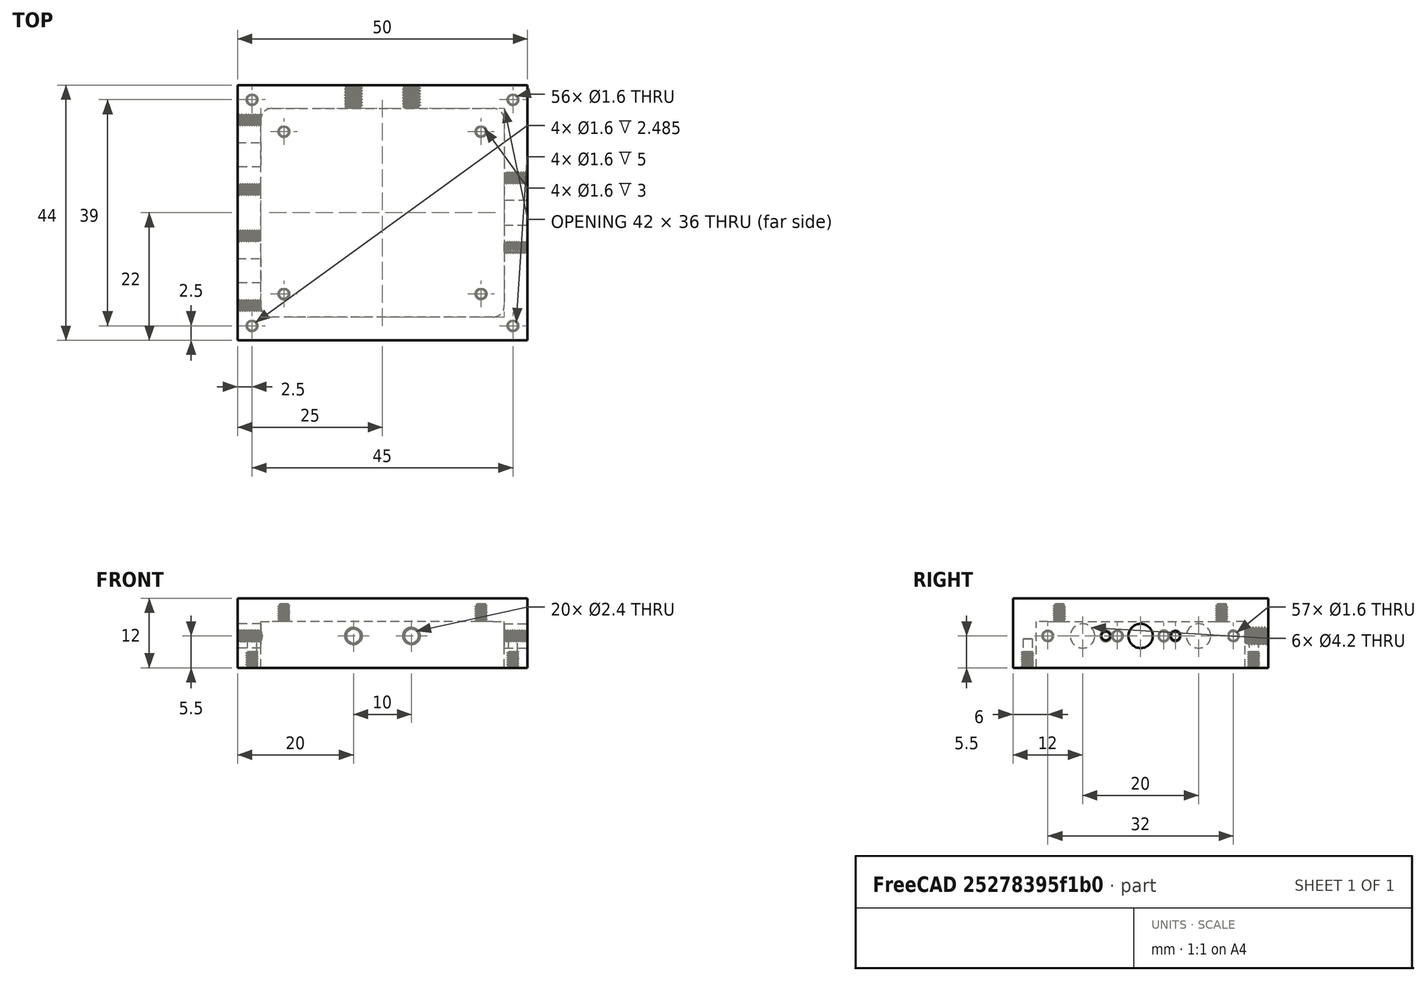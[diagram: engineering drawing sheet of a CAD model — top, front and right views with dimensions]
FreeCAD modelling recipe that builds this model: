
FCSTD DOCUMENT  (FreeCAD 0.19R24291 (Git))
Label: shell
License: All rights reserved
LicenseURL: http://en.wikipedia.org/wiki/All_rights_reserved
objects: TechDraw::DrawViewDimension×31, Part::FeaturePython×16, Sketcher::SketchObject×8, PartDesign::Pocket×7, TechDraw::DrawProjGroupItem×4, Part::MultiFuse×3, PartDesign::Pad×1, PartDesign::Body×1, TechDraw::DrawSVGTemplate×1, TechDraw::DrawProjGroup×1, TechDraw::DrawViewSection×1, TechDraw::DrawPage×1, Part::Cut×1
note: 45 computed .brp shape members not serialized (recipe doc carries the construction recipe); baked Part::Feature solids carry a one-line shape summary decoded from their .brp

FEATURE [Sketcher::SketchObject] Sketch
  FullyConstrained = true
  MapMode = 5
  Support = -> [XY_Plane]
  sketch-geometry (4):
    g0: LineSegment StartX=0 StartY=0 StartZ=0 EndX=50 EndY=0 EndZ=0
    g1: LineSegment StartX=50 StartY=0 StartZ=0 EndX=50 EndY=-44 EndZ=0
    g2: LineSegment StartX=50 StartY=-44 StartZ=0 EndX=0 EndY=-44 EndZ=0
    g3: LineSegment StartX=0 StartY=-44 StartZ=0 EndX=0 EndY=0 EndZ=0
  constraints (11):
    c: Coincident(g0,g1)
    c: Coincident(g1,g2)
    c: Coincident(g2,g3)
    c: Coincident(g3,g0)
    c: Horizontal(g0)
    c: Horizontal(g2)
    c: Vertical(g1)
    c: Vertical(g3)
    c: Coincident(g0,g-1)
    c: DistanceX(g2,g2) = 50
    c: DistanceY(g1,g1) = 44
FEATURE [PartDesign::Pad] Pad
  Direction = (1,1,1)
  Length = 12
  Length2 = 100
  Profile = -> Sketch
  Type = 0
FEATURE [Sketcher::SketchObject] Sketch001
  FullyConstrained = true
  MapMode = 5
  Support = -> [XY_Plane]
  sketch-geometry (8):
    g0: LineSegment StartX=6 StartY=-4 StartZ=0 EndX=44 EndY=-4 EndZ=0
    g1: LineSegment StartX=46 StartY=-6 StartZ=0 EndX=46 EndY=-38 EndZ=0
    g2: LineSegment StartX=44 StartY=-40 StartZ=0 EndX=6 EndY=-40 EndZ=0
    g3: LineSegment StartX=4 StartY=-38 StartZ=0 EndX=4 EndY=-6 EndZ=0
    g4: ArcOfCircle CenterX=6 CenterY=-6 CenterZ=0 NormalX=0 NormalY=0 NormalZ=1 AngleXU=0 Radius=2 StartAngle=1.5708 EndAngle=3.14159
    g5: ArcOfCircle CenterX=44 CenterY=-6 CenterZ=0 NormalX=0 NormalY=0 NormalZ=1 AngleXU=0 Radius=2 StartAngle=0 EndAngle=1.5708
    g6: ArcOfCircle CenterX=44 CenterY=-38 CenterZ=0 NormalX=0 NormalY=0 NormalZ=1 AngleXU=0 Radius=2 StartAngle=4.71239 EndAngle=6.28319
    g7: ArcOfCircle CenterX=6 CenterY=-38 CenterZ=0 NormalX=0 NormalY=0 NormalZ=1 AngleXU=0 Radius=2 StartAngle=3.14159 EndAngle=4.71239
  constraints (20):
    c: Horizontal(g0)
    c: Horizontal(g2)
    c: Vertical(g1)
    c: Vertical(g3)
    c: Tangent(g0,g4) = 1.5708
    c: Tangent(g3,g4) = 1.5708
    c: Tangent(g0,g5) = 1.5708
    c: Tangent(g1,g5) = 1.5708
    c: Tangent(g1,g6) = 1.5708
    c: Tangent(g2,g6) = 1.5708
    c: Tangent(g2,g7) = 1.5708
    c: Tangent(g3,g7) = 1.5708
    c: Radius(g5) = 2
    c: Radius(g6) = 2
    c: Radius(g4) = 2
    c: Radius(g7) = 2
    c: DistanceX(g3) = 4
    c: DistanceY(g0) = -4
    c: DistanceX(g1) = 46
    c: DistanceY(g2) = -40
FEATURE [PartDesign::Pocket] Pocket
  BaseFeature = -> Pad
  Length = 8
  Length2 = 100
  Profile = -> Sketch001
  Reversed = true
  Type = 0
FEATURE [Sketcher::SketchObject] Sketch011
  FullyConstrained = true
  MapMode = 5
  Placement = pos=(0,0,0) rot=(0.57735,0.57735,0.57735;2.0944rad)
  Support = -> [YZ_Plane]
  sketch-geometry (2):
    g0: Circle CenterX=-32 CenterY=5.5 CenterZ=0 NormalX=0 NormalY=0 NormalZ=1 AngleXU=0 Radius=2.1
    g1: Circle CenterX=-12 CenterY=5.5 CenterZ=0 NormalX=0 NormalY=0 NormalZ=1 AngleXU=0 Radius=2.1
  constraints (6):
    c: Diameter(g0) = 4.2
    c: DistanceY(g0) = 5.5
    c: DistanceY(g1) = 5.5
    c: DistanceX(g1) = -12
    c: DistanceX(g0) = -32
    c: Diameter(g1) = 4.2
FEATURE [PartDesign::Pocket] Pocket001
  BaseFeature = -> Pocket
  Length = 0
  Length2 = 100
  Profile = -> Sketch011
  Reversed = true
  Type = 3
  UpToFace = -> Pocket [Face7]
FEATURE [Sketcher::SketchObject] Sketch012
  FullyConstrained = true
  MapMode = 5
  Placement = pos=(0,0,0) rot=(0.57735,-0.57735,-0.57735;2.0944rad)
  Support = -> [Pocket001]
  sketch-geometry (4):
    g0: Circle CenterX=6 CenterY=5.5 CenterZ=0 NormalX=0 NormalY=0 NormalZ=1 AngleXU=0 Radius=0.8
    g1: Circle CenterX=18 CenterY=5.5 CenterZ=0 NormalX=0 NormalY=0 NormalZ=1 AngleXU=0 Radius=0.8
    g2: Circle CenterX=26 CenterY=5.5 CenterZ=0 NormalX=0 NormalY=0 NormalZ=1 AngleXU=0 Radius=0.8
    g3: Circle CenterX=38 CenterY=5.5 CenterZ=0 NormalX=0 NormalY=0 NormalZ=1 AngleXU=0 Radius=0.8
  constraints (12):
    c: Diameter(g0) = 1.6
    c: Diameter(g1) = 1.6
    c: Diameter(g2) = 1.6
    c: Diameter(g3) = 1.6
    c: DistanceY(g0) = 5.5
    c: DistanceY(g1) = 5.5
    c: DistanceY(g2) = 5.5
    c: DistanceY(g3) = 5.5
    c: DistanceX(g0,g1) = 12
    c: DistanceX(g2,g3) = 12
    c: DistanceX(g1,g2) = 8
    c: DistanceX(g0) = 6
FEATURE [PartDesign::Pocket] Pocket002
  BaseFeature = -> Pocket001
  Length = 5
  Length2 = 100
  Profile = -> Sketch012
  Type = 0
FEATURE [Sketcher::SketchObject] Sketch013
  FullyConstrained = true
  MapMode = 5
  Placement = pos=(50,0,0) rot=(0.57735,0.57735,0.57735;2.0944rad)
  Support = -> [Pocket002]
  sketch-geometry (3):
    g0: Circle CenterX=-22 CenterY=5.5 CenterZ=0 NormalX=0 NormalY=0 NormalZ=1 AngleXU=0 Radius=2.1
    g1: Circle CenterX=-28 CenterY=5.5 CenterZ=0 NormalX=0 NormalY=0 NormalZ=1 AngleXU=0 Radius=0.75
    g2: Circle CenterX=-16 CenterY=5.5 CenterZ=0 NormalX=0 NormalY=0 NormalZ=1 AngleXU=0 Radius=0.8
  constraints (9):
    c: Diameter(g0) = 4.2
    c: Diameter(g2) = 1.6
    c: Diameter(g1) = 1.5
    c: DistanceY(g1) = 5.5
    c: DistanceY(g0) = 5.5
    c: DistanceY(g2) = 5.5
    c: DistanceX(g1,g2) = 12
    c: DistanceX(g0,g2) = 6
    c: DistanceX(g0) = -22
FEATURE [PartDesign::Pocket] Pocket003
  BaseFeature = -> Pocket002
  Length = 4
  Length2 = 100
  Profile = -> Sketch013
  Type = 0
FEATURE [Sketcher::SketchObject] Sketch015
  FullyConstrained = true
  MapMode = 5
  Support = -> [XY_Plane]
  sketch-geometry (4):
    g0: Circle CenterX=2.5 CenterY=-2.5 CenterZ=0 NormalX=0 NormalY=0 NormalZ=1 AngleXU=0 Radius=0.8
    g1: Circle CenterX=2.5 CenterY=-41.5 CenterZ=0 NormalX=0 NormalY=0 NormalZ=1 AngleXU=0 Radius=0.8
    g2: Circle CenterX=47.5 CenterY=-41.5 CenterZ=0 NormalX=0 NormalY=0 NormalZ=1 AngleXU=0 Radius=0.8
    g3: Circle CenterX=47.5 CenterY=-2.5 CenterZ=0 NormalX=0 NormalY=0 NormalZ=1 AngleXU=0 Radius=0.8
  constraints (12):
    c: Diameter(g0) = 1.6
    c: Diameter(g1) = 1.6
    c: Diameter(g2) = 1.6
    c: Diameter(g3) = 1.6
    c: DistanceX(g0) = 2.5
    c: DistanceY(g0) = -2.5
    c: DistanceY(g3) = -2.5
    c: DistanceX(g3) = 47.5
    c: DistanceY(g1) = -41.5
    c: DistanceX(g1) = 2.5
    c: DistanceX(g2) = 47.5
    c: DistanceY(g2) = -41.5
FEATURE [PartDesign::Pocket] Pocket005
  BaseFeature = -> Pocket003
  Length = 5
  Length2 = 100
  Profile = -> Sketch015
  Reversed = true
  Type = 0
FEATURE [Sketcher::SketchObject] Sketch017
  FullyConstrained = true
  MapMode = 5
  Placement = pos=(0,0,0) rot=(1,0,0;1.5708rad)
  Support = -> [XZ_Plane]
  sketch-geometry (2):
    g0: Circle CenterX=20 CenterY=5.5 CenterZ=0 NormalX=0 NormalY=0 NormalZ=1 AngleXU=0 Radius=1.2
    g1: Circle CenterX=30 CenterY=5.5 CenterZ=0 NormalX=0 NormalY=0 NormalZ=1 AngleXU=0 Radius=1.2
  constraints (6):
    c: Diameter(g0) = 2.4
    c: Diameter(g1) = 2.4
    c: DistanceY(g0) = 5.5
    c: DistanceY(g1) = 5.5
    c: DistanceX(g0,g1) = 10
    c: DistanceX(g0) = 20
FEATURE [PartDesign::Pocket] Pocket007
  BaseFeature = -> Pocket005
  Length = 4
  Length2 = 100
  Profile = -> Sketch017
  Reversed = true
  Type = 0
FEATURE [Sketcher::SketchObject] Sketch018
  FullyConstrained = true
  MapMode = 5
  Support = -> [XY_Plane]
  sketch-geometry (4):
    g0: Circle CenterX=8 CenterY=-36 CenterZ=0 NormalX=0 NormalY=0 NormalZ=1 AngleXU=0 Radius=0.8
    g1: Circle CenterX=42 CenterY=-36 CenterZ=0 NormalX=0 NormalY=0 NormalZ=1 AngleXU=0 Radius=0.8
    g2: Circle CenterX=8 CenterY=-8 CenterZ=0 NormalX=0 NormalY=0 NormalZ=1 AngleXU=0 Radius=0.8
    g3: Circle CenterX=42 CenterY=-8 CenterZ=0 NormalX=0 NormalY=0 NormalZ=1 AngleXU=0 Radius=0.8
  constraints (12):
    c: Diameter(g2) = 1.6
    c: Diameter(g3) = 1.6
    c: Diameter(g1) = 1.6
    c: Diameter(g0) = 1.6
    c: DistanceX(g0) = 8
    c: DistanceY(g0) = -36
    c: DistanceX(g1) = 42
    c: DistanceY(g1) = -36
    c: DistanceY(g2) = -8
    c: DistanceX(g2) = 8
    c: DistanceX(g3) = 42
    c: DistanceY(g3) = -8
FEATURE [PartDesign::Pocket] Pocket008
  BaseFeature = -> Pocket007
  Length = 11
  Length2 = 100
  Profile = -> Sketch018
  Reversed = true
  Type = 0
FEATURE [PartDesign::Body] Body
  Group = -> [Sketch,Pad,Sketch001,Pocket,Sketch011,Pocket001,Sketch012,Pocket002,Sketch013,Pocket003,Sketch015,Pocket005,Sketch017,Pocket007,Sketch018,Pocket008]
  Origin = -> Origin
  Tip = -> Pocket008
FEATURE [TechDraw::DrawSVGTemplate] Template
  EditableTexts = Designed_by_Name=YXK; FC-Date=2021/9/6; FC-Title=Title; Subtitle=DiffAD620_shell
  Height = 210
  Orientation = 1
  Width = 297
FEATURE [TechDraw::DrawProjGroupItem] ProjItem  label="Front"
  CoarseView = false
  Direction = (0,0,-1)
  Focus = 100
  HardHidden = false
  IsoCount = 0
  IsoHidden = false
  IsoVisible = false
  LockPosition = true
  Perspective = false
  Rotation = 0
  RotationVector = (1,0,0)
  Scale = 1.5
  ScaleType = 2
  SeamHidden = false
  SeamVisible = true
  SmoothHidden = false
  SmoothVisible = true
  Source = -> [Pocket008]
  Type = 0
  X = 0
  XDirection = (1,0,0)
  Y = 0
FEATURE [TechDraw::DrawProjGroupItem] ProjItem001  label="Left"
  CoarseView = false
  Direction = (-1,0,-1e-16)
  Focus = 100
  HardHidden = false
  IsoCount = 0
  IsoHidden = false
  IsoVisible = false
  LockPosition = false
  Perspective = false
  Rotation = 0
  RotationVector = (1,0,0)
  Scale = 1.5
  ScaleType = 2
  SeamHidden = false
  SeamVisible = true
  SmoothHidden = false
  SmoothVisible = true
  Source = -> [Pocket008]
  Type = 1
  X = 88.5544
  XDirection = (1e-16,0,-1)
  Y = 0
FEATURE [TechDraw::DrawProjGroupItem] ProjItem002  label="Right"
  CoarseView = false
  Direction = (1,0,-1e-16)
  Focus = 100
  HardHidden = false
  IsoCount = 0
  IsoHidden = false
  IsoVisible = false
  LockPosition = false
  Perspective = false
  Rotation = 0
  RotationVector = (1,0,0)
  Scale = 1.5
  ScaleType = 2
  SeamHidden = false
  SeamVisible = true
  SmoothHidden = false
  SmoothVisible = true
  Source = -> [Pocket008]
  Type = 2
  X = -87.7386
  XDirection = (1e-16,0,1)
  Y = 0
FEATURE [TechDraw::DrawProjGroupItem] ProjItem003  label="FrontTopRight"
  CoarseView = false
  Direction = (0.57735,-0.57735,-0.57735)
  Focus = 100
  HardHidden = false
  IsoCount = 0
  IsoHidden = false
  IsoVisible = false
  LockPosition = false
  Perspective = false
  Rotation = 0
  RotationVector = (1,0,0)
  Scale = 1.5
  ScaleType = 2
  SeamHidden = false
  SeamVisible = true
  SmoothHidden = false
  SmoothVisible = true
  Source = -> [Pocket008]
  Type = 7
  X = -105.359
  XDirection = (0.707107,0,0.707107)
  Y = -87.1945
FEATURE [TechDraw::DrawProjGroup] ProjGroup
  Anchor = -> ProjItem
  AutoDistribute = false
  LockPosition = false
  ProjectionType = 0
  Rotation = 0
  Scale = 1.5
  ScaleType = 2
  Source = -> [Pocket008]
  Views = -> [ProjItem,ProjItem001,ProjItem002,ProjItem003]
  X = 158.446
  Y = 149.013
  spacingX = 15
  spacingY = 15
FEATURE [TechDraw::DrawViewDimension] Dimension
  Arbitrary = false
  ArbitraryTolerances = false
  EqualTolerance = true
  FormatSpec = %.0f
  FormatSpecOverTolerance = %+.2f
  FormatSpecUnderTolerance = %+.2f
  Inverted = false
  LockPosition = false
  MeasureType = 1
  OverTolerance = 0
  References2D = -> [ProjItem]
  Rotation = 0
  ScaleType = 0
  TheoreticalExact = false
  Type = 1
  UnderTolerance = 0
  X = -1.51058
  Y = -14.761
FEATURE [TechDraw::DrawViewDimension] Dimension001
  Arbitrary = false
  ArbitraryTolerances = false
  EqualTolerance = true
  FormatSpec = %.0f
  FormatSpecOverTolerance = %+.2f
  FormatSpecUnderTolerance = %+.2f
  Inverted = false
  LockPosition = false
  MeasureType = 1
  OverTolerance = 0
  References2D = -> [ProjItem]
  Rotation = 0
  ScaleType = 0
  TheoreticalExact = false
  Type = 2
  UnderTolerance = 0
  X = 22.5074
  Y = 3.51417
FEATURE [TechDraw::DrawViewDimension] Dimension002
  Arbitrary = false
  ArbitraryTolerances = false
  EqualTolerance = true
  FormatSpec = %.0f
  FormatSpecOverTolerance = %+.2f
  FormatSpecUnderTolerance = %+.2f
  Inverted = false
  LockPosition = false
  MeasureType = 1
  OverTolerance = 0
  References2D = -> [ProjItem]
  Rotation = 0
  ScaleType = 0
  TheoreticalExact = false
  Type = 1
  UnderTolerance = 0
  X = -1.46443
  Y = -41.4304
FEATURE [TechDraw::DrawViewDimension] Dimension003
  Arbitrary = false
  ArbitraryTolerances = false
  EqualTolerance = true
  FormatSpec = %.0f
  FormatSpecOverTolerance = %+.2f
  FormatSpecUnderTolerance = %+.2f
  Inverted = false
  LockPosition = false
  MeasureType = 1
  OverTolerance = 0
  References2D = -> [ProjItem]
  Rotation = 0
  ScaleType = 0
  TheoreticalExact = false
  Type = 2
  UnderTolerance = 0
  X = 51.9622
  Y = -1.04489
FEATURE [TechDraw::DrawViewDimension] Dimension004
  Arbitrary = false
  ArbitraryTolerances = false
  EqualTolerance = true
  FormatSpec = %.0f
  FormatSpecOverTolerance = %+.2f
  FormatSpecUnderTolerance = %+.2f
  Inverted = false
  LockPosition = false
  MeasureType = 1
  OverTolerance = 0
  References2D = -> [ProjItem]
  Rotation = 0
  ScaleType = 0
  TheoreticalExact = false
  Type = 1
  UnderTolerance = 0
  X = -43.6818
  Y = -32.9738
FEATURE [TechDraw::DrawViewDimension] Dimension005
  Arbitrary = false
  ArbitraryTolerances = false
  EqualTolerance = true
  FormatSpec = %.0f
  FormatSpecOverTolerance = %+.2f
  FormatSpecUnderTolerance = %+.2f
  Inverted = false
  LockPosition = false
  MeasureType = 1
  OverTolerance = 0
  References2D = -> [ProjItem]
  Rotation = 0
  ScaleType = 0
  TheoreticalExact = false
  Type = 2
  UnderTolerance = 0
  X = 41.6799
  Y = -20.2635
FEATURE [TechDraw::DrawViewDimension] Dimension006
  Arbitrary = false
  ArbitraryTolerances = false
  EqualTolerance = true
  FormatSpec = %.0f
  FormatSpecOverTolerance = %+.2f
  FormatSpecUnderTolerance = %+.2f
  Inverted = false
  LockPosition = false
  MeasureType = 1
  OverTolerance = 0
  References2D = -> [ProjItem001]
  Rotation = 0
  ScaleType = 0
  TheoreticalExact = false
  Type = 1
  UnderTolerance = 0
  X = -0.151106
  Y = -46.1582
FEATURE [TechDraw::DrawViewDimension] Dimension007
  Arbitrary = false
  ArbitraryTolerances = false
  EqualTolerance = true
  FormatSpec = %.1f
  FormatSpecOverTolerance = %+.2f
  FormatSpecUnderTolerance = %+.2f
  Inverted = false
  LockPosition = false
  MeasureType = 1
  OverTolerance = 0
  References2D = -> [ProjItem]
  Rotation = 0
  ScaleType = 0
  TheoreticalExact = false
  Type = 1
  UnderTolerance = 0
  X = 27.4267
  Y = 44.2346
FEATURE [TechDraw::DrawViewDimension] Dimension008
  Arbitrary = false
  ArbitraryTolerances = false
  EqualTolerance = true
  FormatSpec = %.1f
  FormatSpecOverTolerance = %+.2f
  FormatSpecUnderTolerance = %+.2f
  Inverted = false
  LockPosition = false
  MeasureType = 1
  OverTolerance = 0
  References2D = -> [ProjItem]
  Rotation = 0
  ScaleType = 0
  TheoreticalExact = false
  Type = 2
  UnderTolerance = 0
  X = 42.6656
  Y = 25.7621
FEATURE [TechDraw::DrawViewDimension] Dimension009
  Arbitrary = false
  ArbitraryTolerances = false
  EqualTolerance = true
  FormatSpec = %.0f
  FormatSpecOverTolerance = %+.2f
  FormatSpecUnderTolerance = %+.2f
  Inverted = false
  LockPosition = false
  MeasureType = 1
  OverTolerance = 0
  References2D = -> [ProjItem]
  Rotation = 0
  ScaleType = 0
  TheoreticalExact = false
  Type = 1
  UnderTolerance = 0
  X = -27.8145
  Y = 16.2307
FEATURE [TechDraw::DrawViewDimension] Dimension010
  Arbitrary = false
  ArbitraryTolerances = false
  EqualTolerance = true
  FormatSpec = %.0f
  FormatSpecOverTolerance = %+.2f
  FormatSpecUnderTolerance = %+.2f
  Inverted = false
  LockPosition = false
  MeasureType = 1
  OverTolerance = 0
  References2D = -> [ProjItem]
  Rotation = 0
  ScaleType = 0
  TheoreticalExact = false
  Type = 2
  UnderTolerance = 0
  X = -19.6538
  Y = 26.0273
FEATURE [TechDraw::DrawViewDimension] Dimension011
  Arbitrary = false
  ArbitraryTolerances = false
  EqualTolerance = true
  FormatSpec = R%.0f
  FormatSpecOverTolerance = %+.2f
  FormatSpecUnderTolerance = %+.2f
  Inverted = false
  LockPosition = false
  MeasureType = 1
  OverTolerance = 0
  References2D = -> [ProjItem]
  Rotation = 0
  ScaleType = 0
  TheoreticalExact = false
  Type = 4
  UnderTolerance = 0
  X = -33.2413
  Y = 46.5037
FEATURE [TechDraw::DrawViewDimension] Dimension012
  Arbitrary = true
  ArbitraryTolerances = false
  EqualTolerance = true
  FormatSpec = 4xM2深3
  FormatSpecOverTolerance = %+.2f
  FormatSpecUnderTolerance = %+.2f
  Inverted = false
  LockPosition = false
  MeasureType = 1
  OverTolerance = 0
  References2D = -> [ProjItem]
  Rotation = 0
  ScaleType = 0
  TheoreticalExact = false
  Type = 5
  UnderTolerance = 0
  X = -57.0458
  Y = -14.32
FEATURE [TechDraw::DrawViewDimension] Dimension013
  Arbitrary = true
  ArbitraryTolerances = false
  EqualTolerance = true
  FormatSpec = 4xM2深3
  FormatSpecOverTolerance = %+.2f
  FormatSpecUnderTolerance = %+.2f
  Inverted = false
  LockPosition = false
  MeasureType = 1
  OverTolerance = 0
  References2D = -> [ProjItem]
  Rotation = 0
  ScaleType = 0
  TheoreticalExact = false
  Type = 5
  UnderTolerance = 0
  X = -58.3902
  Y = -2.55251
FEATURE [TechDraw::DrawViewDimension] Dimension014
  Arbitrary = false
  ArbitraryTolerances = false
  EqualTolerance = true
  FormatSpec = %.0f
  FormatSpecOverTolerance = %+.2f
  FormatSpecUnderTolerance = %+.2f
  Inverted = false
  LockPosition = false
  MeasureType = 1
  OverTolerance = 0
  References2D = -> [ProjItem002]
  Rotation = 0
  ScaleType = 0
  TheoreticalExact = false
  Type = 2
  UnderTolerance = 0
  X = -26.1138
  Y = -2.16784
FEATURE [TechDraw::DrawViewDimension] Dimension015
  Arbitrary = false
  ArbitraryTolerances = false
  EqualTolerance = true
  FormatSpec = %.0f
  FormatSpecOverTolerance = %+.2f
  FormatSpecUnderTolerance = %+.2f
  Inverted = false
  LockPosition = false
  MeasureType = 1
  OverTolerance = 0
  References2D = -> [ProjItem002]
  Rotation = 0
  ScaleType = 0
  TheoreticalExact = false
  Type = 2
  UnderTolerance = 0
  X = -19.1767
  Y = -2.33216
FEATURE [TechDraw::DrawViewDimension] Dimension016
  Arbitrary = false
  ArbitraryTolerances = false
  EqualTolerance = true
  FormatSpec = ⌀%.1f
  FormatSpecOverTolerance = %+.2f
  FormatSpecUnderTolerance = %+.2f
  Inverted = false
  LockPosition = false
  MeasureType = 1
  OverTolerance = 0
  References2D = -> [ProjItem002]
  Rotation = 0
  ScaleType = 0
  TheoreticalExact = false
  Type = 5
  UnderTolerance = 0
  X = 19.2938
  Y = 22.3288
FEATURE [TechDraw::DrawViewDimension] Dimension017
  Arbitrary = true
  ArbitraryTolerances = false
  EqualTolerance = true
  FormatSpec = 2xM2
  FormatSpecOverTolerance = %+.2f
  FormatSpecUnderTolerance = %+.2f
  Inverted = false
  LockPosition = false
  MeasureType = 1
  OverTolerance = 0
  References2D = -> [ProjItem002]
  Rotation = 0
  ScaleType = 0
  TheoreticalExact = false
  Type = 5
  UnderTolerance = 0
  X = 27.3148
  Y = 13.6574
FEATURE [TechDraw::DrawViewDimension] Dimension018
  Arbitrary = false
  ArbitraryTolerances = false
  EqualTolerance = true
  FormatSpec = %.0f
  FormatSpecOverTolerance = %+.2f
  FormatSpecUnderTolerance = %+.2f
  Inverted = false
  LockPosition = false
  MeasureType = 1
  OverTolerance = 0
  References2D = -> [ProjItem001]
  Rotation = 0
  ScaleType = 0
  TheoreticalExact = false
  Type = 2
  UnderTolerance = 0
  X = 29.6044
  Y = 15
FEATURE [TechDraw::DrawViewDimension] Dimension019
  Arbitrary = false
  ArbitraryTolerances = false
  EqualTolerance = true
  FormatSpec = %.0f
  FormatSpecOverTolerance = %+.2f
  FormatSpecUnderTolerance = %+.2f
  Inverted = false
  LockPosition = false
  MeasureType = 1
  OverTolerance = 0
  References2D = -> [ProjItem001]
  Rotation = 0
  ScaleType = 0
  TheoreticalExact = false
  Type = 2
  UnderTolerance = 0
  X = 18.4673
  Y = 0.825165
FEATURE [TechDraw::DrawViewDimension] Dimension020
  Arbitrary = false
  ArbitraryTolerances = false
  EqualTolerance = true
  FormatSpec = %.0f
  FormatSpecOverTolerance = %+.2f
  FormatSpecUnderTolerance = %+.2f
  Inverted = false
  LockPosition = false
  MeasureType = 1
  OverTolerance = 0
  References2D = -> [ProjItem001]
  Rotation = 0
  ScaleType = 0
  TheoreticalExact = false
  Type = 2
  UnderTolerance = 0
  X = 29.9083
  Y = -15.8782
FEATURE [TechDraw::DrawViewDimension] Dimension021
  Arbitrary = false
  ArbitraryTolerances = false
  EqualTolerance = true
  FormatSpec = %.0f
  FormatSpecOverTolerance = %+.2f
  FormatSpecUnderTolerance = %+.2f
  Inverted = false
  LockPosition = false
  MeasureType = 1
  OverTolerance = 0
  References2D = -> [ProjItem001]
  Rotation = 0
  ScaleType = 0
  TheoreticalExact = false
  Type = 2
  UnderTolerance = 0
  X = 18.1756
  Y = 11.9189
FEATURE [TechDraw::DrawViewDimension] Dimension022
  Arbitrary = false
  ArbitraryTolerances = false
  EqualTolerance = true
  FormatSpec = %.0f
  FormatSpecOverTolerance = %+.2f
  FormatSpecUnderTolerance = %+.2f
  Inverted = false
  LockPosition = false
  MeasureType = 1
  OverTolerance = 0
  References2D = -> [ProjItem001]
  Rotation = 0
  ScaleType = 0
  TheoreticalExact = false
  Type = 2
  UnderTolerance = 0
  X = 18.3011
  Y = -8.20297
FEATURE [TechDraw::DrawViewDimension] Dimension023
  Arbitrary = true
  ArbitraryTolerances = false
  EqualTolerance = true
  FormatSpec = 4xM2
  FormatSpecOverTolerance = %+.2f
  FormatSpecUnderTolerance = %+.2f
  Inverted = false
  LockPosition = false
  MeasureType = 1
  OverTolerance = 0
  References2D = -> [ProjItem001]
  Rotation = 0
  ScaleType = 0
  TheoreticalExact = false
  Type = 5
  UnderTolerance = 0
  X = -22.3308
  Y = 36.758
FEATURE [TechDraw::DrawViewDimension] Dimension024
  Arbitrary = false
  ArbitraryTolerances = false
  EqualTolerance = true
  FormatSpec = ⌀%.1f
  FormatSpecOverTolerance = %+.2f
  FormatSpecUnderTolerance = %+.2f
  Inverted = false
  LockPosition = false
  MeasureType = 1
  OverTolerance = 0
  References2D = -> [ProjItem001]
  Rotation = 0
  ScaleType = 0
  TheoreticalExact = false
  Type = 5
  UnderTolerance = 0
  X = -22.4562
  Y = 20.6999
FEATURE [TechDraw::DrawViewSection] SectionView  label="Section  - "
  BaseView = -> ProjItem
  CoarseView = false
  CutSurfaceDisplay = 2
  Direction = (0,-1,0)
  FileGeomPattern = <path>
  FileHatchPattern = <path>
  Focus = 100
  FuseBeforeCut = false
  HardHidden = false
  HatchScale = 1
  IsoCount = 0
  IsoHidden = false
  IsoVisible = false
  LockPosition = false
  NameGeomPattern = Diamond
  Perspective = false
  Rotation = 0
  Scale = 1.5
  ScaleType = 0
  SeamHidden = false
  SeamVisible = true
  SectionDirection = 3
  SectionNormal = (0,-1,0)
  SectionOrigin = (25,-17,6)
  SmoothHidden = false
  SmoothVisible = true
  Source = -> [Pocket008]
  X = 158.197
  XDirection = (1,0,0)
  Y = 79.0756
FEATURE [TechDraw::DrawViewDimension] Dimension025
  Arbitrary = false
  ArbitraryTolerances = false
  EqualTolerance = true
  FormatSpec = %.0f
  FormatSpecOverTolerance = %+.2f
  FormatSpecUnderTolerance = %+.2f
  Inverted = false
  LockPosition = false
  MeasureType = 1
  OverTolerance = 0
  References2D = -> [SectionView]
  Rotation = 0
  ScaleType = 0
  TheoreticalExact = false
  Type = 2
  UnderTolerance = 0
  X = 43.1667
  Y = -1.20794
FEATURE [Part::FeaturePython] ThreadedRod  label="M2x3.0-ThreadedRod"  # Fasteners workbench fastener (typed FeaturePython)
  Placement = pos=(47.5,-41.5,0) rot=(-1,0,0;3.14159rad)
  baseObject = -> Body [Edge18]
  diameter = 2
  invert = true
  length = 3
  matchOuter = false
  offset = 0
  thread = true
FEATURE [Part::FeaturePython] ThreadedRod001  label="M2x3.0-ThreadedRod008"  # Fasteners workbench fastener (typed FeaturePython)
  Placement = pos=(47.5,-2.5,0) rot=(-1,0,0;3.14159rad)
  baseObject = -> Body [Edge28]
  diameter = 2
  invert = true
  length = 3
  matchOuter = false
  offset = 0
  thread = true
FEATURE [Part::FeaturePython] ThreadedRod002  label="M2x3.0-ThreadedRod009"  # Fasteners workbench fastener (typed FeaturePython)
  Placement = pos=(42,-8,8) rot=(-1,0,0;3.14159rad)
  baseObject = -> Body [Edge90]
  diameter = 2
  invert = false
  length = 3
  matchOuter = false
  offset = 0
  thread = true
FEATURE [Part::FeaturePython] ThreadedRod003  label="M2x3.0-ThreadedRod010"  # Fasteners workbench fastener (typed FeaturePython)
  Placement = pos=(42,-36,8) rot=(-1,0,0;3.14159rad)
  baseObject = -> Body [Edge88]
  diameter = 2
  invert = false
  length = 3
  matchOuter = false
  offset = 0
  thread = true
FEATURE [Part::FeaturePython] ThreadedRod004  label="M2x3.0-ThreadedRod011"  # Fasteners workbench fastener (typed FeaturePython)
  Placement = pos=(8,-36,8) rot=(-1,0,0;3.14159rad)
  baseObject = -> Body [Edge89]
  diameter = 2
  invert = false
  length = 3
  matchOuter = false
  offset = 0
  thread = true
FEATURE [Part::FeaturePython] ThreadedRod005  label="M2x3.0-ThreadedRod012"  # Fasteners workbench fastener (typed FeaturePython)
  Placement = pos=(8,-8,8) rot=(-1,0,0;3.14159rad)
  baseObject = -> Body [Edge91]
  diameter = 2
  invert = false
  length = 3
  matchOuter = false
  offset = 0
  thread = true
FEATURE [Part::FeaturePython] ThreadedRod006  label="M2x3.0-ThreadedRod013"  # Fasteners workbench fastener (typed FeaturePython)
  Placement = pos=(2.5,-2.5,0) rot=(-1,0,0;3.14159rad)
  baseObject = -> Body [Edge29]
  diameter = 2
  invert = true
  length = 3
  matchOuter = false
  offset = 0
  thread = true
FEATURE [Part::FeaturePython] ThreadedRod007  label="M2x3.0-ThreadedRod014"  # Fasteners workbench fastener (typed FeaturePython)
  Placement = pos=(2.5,-41.5,0) rot=(-1,0,0;3.14159rad)
  baseObject = -> Body [Edge19]
  diameter = 2
  invert = true
  length = 3
  matchOuter = false
  offset = 0
  thread = true
FEATURE [Part::FeaturePython] ThreadedRod008  label="M2x4.0-ThreadedRod"  # Fasteners workbench fastener (typed FeaturePython)
  Placement = pos=(50,-28,5.5) rot=(0,1,0;1.5708rad)
  baseObject = -> Body [Edge35]
  diameter = 2
  invert = false
  length = 4
  matchOuter = false
  offset = 0
  thread = true
FEATURE [Part::FeaturePython] ThreadedRod009  label="M2x4.0-ThreadedRod006"  # Fasteners workbench fastener (typed FeaturePython)
  Placement = pos=(50,-16,5.5) rot=(0,1,0;1.5708rad)
  baseObject = -> Body [Edge33]
  diameter = 2
  invert = false
  length = 4
  matchOuter = false
  offset = 0
  thread = true
FEATURE [Part::FeaturePython] ThreadedRod010  label="M2x4.0-ThreadedRod007"  # Fasteners workbench fastener (typed FeaturePython)
  Placement = pos=(4,-26,5.5) rot=(0,1,0;1.5708rad)
  baseObject = -> Body [Edge47]
  diameter = 2
  invert = true
  length = 4
  matchOuter = false
  offset = 0
  thread = true
FEATURE [Part::FeaturePython] ThreadedRod011  label="M2x4.0-ThreadedRod008"  # Fasteners workbench fastener (typed FeaturePython)
  Placement = pos=(4,-18,5.5) rot=(0,1,0;1.5708rad)
  baseObject = -> Body [Edge49]
  diameter = 2
  invert = true
  length = 4
  matchOuter = false
  offset = 0
  thread = true
FEATURE [Part::FeaturePython] ThreadedRod012  label="M2x5.0-ThreadedRod"  # Fasteners workbench fastener (typed FeaturePython)
  Placement = pos=(0,-6,5.5) rot=(0,-1,0;1.5708rad)
  baseObject = -> Body [Edge15]
  diameter = 2
  invert = false
  length = 5
  matchOuter = false
  offset = 0
  thread = true
FEATURE [Part::FeaturePython] ThreadedRod013  label="M2x5.0-ThreadedRod001"  # Fasteners workbench fastener (typed FeaturePython)
  Placement = pos=(0,-38,5.5) rot=(0,-1,0;1.5708rad)
  baseObject = -> Body [Edge11]
  diameter = 2
  invert = false
  length = 5
  matchOuter = false
  offset = 0
  thread = true
FEATURE [Part::MultiFuse] Fusion
  Shapes = -> [ThreadedRod,ThreadedRod001,ThreadedRod002,ThreadedRod003,ThreadedRod004,ThreadedRod005,ThreadedRod006,ThreadedRod007,ThreadedRod008,ThreadedRod009,ThreadedRod010,ThreadedRod011,ThreadedRod012,ThreadedRod013]
FEATURE [TechDraw::DrawViewDimension] Dimension026
  Arbitrary = false
  ArbitraryTolerances = false
  EqualTolerance = true
  FormatSpec = %.1f
  FormatSpecOverTolerance = %+.2f
  FormatSpecUnderTolerance = %+.2f
  Inverted = false
  LockPosition = false
  MeasureType = 1
  OverTolerance = 0
  References2D = -> [ProjItem001]
  Rotation = 0
  ScaleType = 0
  TheoreticalExact = false
  Type = 1
  UnderTolerance = 0
  X = 18.3887
  Y = -35.4859
FEATURE [TechDraw::DrawViewDimension] Dimension028
  Arbitrary = false
  ArbitraryTolerances = false
  EqualTolerance = true
  FormatSpec = %.0f
  FormatSpecOverTolerance = %+.2f
  FormatSpecUnderTolerance = %+.2f
  Inverted = false
  LockPosition = false
  MeasureType = 1
  OverTolerance = 0
  References2D = -> [SectionView]
  Rotation = 0
  ScaleType = 0
  TheoreticalExact = false
  Type = 1
  UnderTolerance = 0
  X = 0.229046
  Y = 1.42594
FEATURE [TechDraw::DrawViewDimension] Dimension029
  Arbitrary = false
  ArbitraryTolerances = false
  EqualTolerance = true
  FormatSpec = %.1f
  FormatSpecOverTolerance = %+.2f
  FormatSpecUnderTolerance = %+.2f
  Inverted = false
  LockPosition = false
  MeasureType = 1
  OverTolerance = 0
  References2D = -> [SectionView]
  Rotation = 0
  ScaleType = 0
  TheoreticalExact = false
  Type = 2
  UnderTolerance = 0
  X = 20.1759
  Y = -2.58454
FEATURE [TechDraw::DrawViewDimension] Dimension027
  Arbitrary = true
  ArbitraryTolerances = false
  EqualTolerance = true
  FormatSpec = 2xM3
  FormatSpecOverTolerance = %+.2f
  FormatSpecUnderTolerance = %+.2f
  Inverted = false
  LockPosition = false
  MeasureType = 1
  OverTolerance = 0
  References2D = -> [SectionView]
  Rotation = 0
  ScaleType = 0
  TheoreticalExact = false
  Type = 5
  UnderTolerance = 0
  X = 24.5303
  Y = 18.9794
FEATURE [TechDraw::DrawViewDimension] Dimension030
  Arbitrary = false
  ArbitraryTolerances = false
  EqualTolerance = true
  FormatSpec = %.1f
  FormatSpecOverTolerance = %+.2f
  FormatSpecUnderTolerance = %+.2f
  Inverted = false
  LockPosition = false
  MeasureType = 1
  OverTolerance = 0
  References2D = -> [ProjItem002]
  Rotation = 0
  ScaleType = 0
  TheoreticalExact = false
  Type = 1
  UnderTolerance = 0
  X = -19.9921
  Y = -15.5278
FEATURE [TechDraw::DrawPage] Page
  KeepUpdated = true
  NextBalloonIndex = 1
  ProjectionType = 0
  Template = -> Template
  Views = -> [ProjGroup,Dimension,Dimension001,Dimension002,Dimension003,Dimension004,Dimension005,Dimension006,Dimension007,Dimension008,Dimension009,Dimension010,Dimension011,Dimension012,Dimension013,Dimension014,Dimension015,Dimension016,Dimension017,Dimension018,Dimension019,Dimension020,Dimension021,Dimension022,Dimension023,Dimension024,SectionView,Dimension025,Dimension026,Dimension027,Dimension028,+2 more]
FEATURE [Part::FeaturePython] ThreadedRod014  label="M3x4.0-ThreadedRod"  # Fasteners workbench fastener (typed FeaturePython)
  Placement = pos=(20,-1.2e-15,5.5) rot=(-1,0,0;1.5708rad)
  diameter = 4
  invert = true
  length = 4
  matchOuter = false
  offset = 0
  thread = true
FEATURE [Part::FeaturePython] ThreadedRod015  label="M3x4.0-ThreadedRod001"  # Fasteners workbench fastener (typed FeaturePython)
  Placement = pos=(30,-1.2e-15,5.5) rot=(-1,0,0;1.5708rad)
  diameter = 4
  invert = true
  length = 4
  matchOuter = false
  offset = 0
  thread = true
FEATURE [Part::MultiFuse] Fusion001
  Shapes = -> [ThreadedRod014,ThreadedRod015]
FEATURE [Part::MultiFuse] Fusion002
  Shapes = -> [Fusion,Fusion001]
FEATURE [Part::Cut] Cut
  Base = -> Pocket008
  Tool = -> Fusion002
note: 2 file-system paths scrubbed to <path> (originals preserved in the JSON sidecar)
